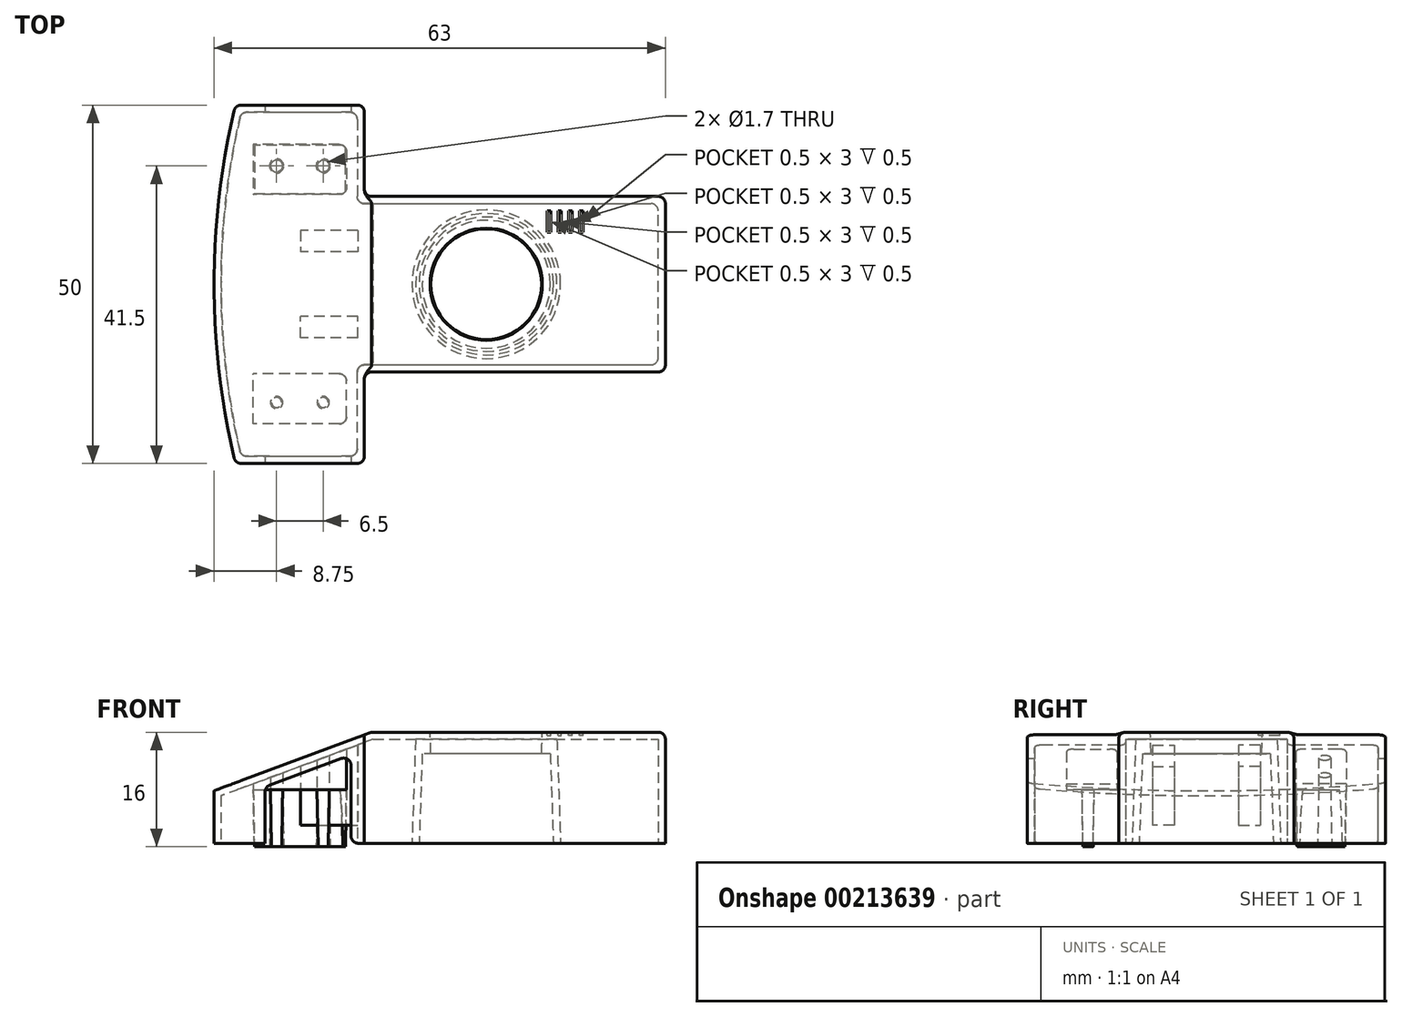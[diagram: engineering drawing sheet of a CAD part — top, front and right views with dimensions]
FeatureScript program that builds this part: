
annotation { "Feature Type Name" : "Feature", "Feature Type Description" : "" }
export const myFeature = defineFeature(function(context is Context, id is Id, definition is map)
    precondition{}
    {
        {
            var Q0;
            Q0=qCreatedBy(makeId("Top.planeOp"),FACE);
            var sketch = newSketch(context, id + "F0", { "sketchPlane" : qUnion([Q0])});
            skCircle(sketch, "E0", {"center": v(-4, 0) * mm, "radius": 9.37 * mm});
            skLineSegment(sketch, "E1.bottom", {"start": v(-21, -12.25) * mm, "end": v(21, -12.25) * mm});
            skLineSegment(sketch, "E1.top", {"start": v(-21, 12.25) * mm, "end": v(21, 12.25) * mm});
            skLineSegment(sketch, "E1.right", {"start": v(21, -12.25) * mm, "end": v(21, 12.25) * mm});
            skLineSegment(sketch, "E2.bottom", {"start": v(-21, -25) * mm, "end": v(-39, -25) * mm});
            skLineSegment(sketch, "E2.top", {"start": v(-21, 25) * mm, "end": v(-39, 25) * mm});
            skLineSegment(sketch, "E2.left", {"start": v(-21, -25) * mm, "end": v(-21, -12.25) * mm});
            skLineSegment(sketch, "E2.right", {"start": v(-39, -25) * mm, "end": v(-39, 25) * mm});
            skPoint(sketch, "E2.middle", {"position": v(-30, 0) * mm});
            skLineSegment(sketch, "E3.trimOffspring", {"start": v(-21, 12.25) * mm, "end": v(-21, 25) * mm});
            skLineSegment(sketch, "E4", {"start": v(-20, 12.25) * mm, "end": v(-20, -12.25) * mm});
            skPoint(sketch, "E5", {"position": v(-42, 0) * mm});
            skPoint(sketch, "E5.positionSnap0", {"position": v(-39, 0) * mm});
            skArc(sketch, "E6", {"start": v(-39, 25) * mm, "mid": v(-42, 0) * mm, "end": v(-39, -25) * mm});
            skSolve(sketch);
        }
        {
            var Q0;
            Q0=qSketchRegion(id+"F0",true);
            var Q1;
            Q1=makeQuery(id+"F0.imprint","IMPRINT",FACE,{"disambiguationData":[TD([[makeQuery(id+"F0.imprint","IMPRINT",EDGE,{"derivedFrom":sQuery(id+"F0.wireOp",EDGE,"E0")}),1.0]])]});
            extrude(context, id + "F1", {"entities" : qUnion([Q0, Q1]), "depth" : 15.5 * mm});
        }
        {
            var Q0;
            Q0=makeQuery(id+"F0.imprint","IMPRINT",FACE,{"disambiguationData":[TD([[makeQuery(id+"F0.imprint","IMPRINT",EDGE,{"derivedFrom":sQuery(id+"F0.wireOp",EDGE,"E0")}),1.0]])]});
            var Q1;
            Q1=makeQuery(id+"F1.opExtrude","CAP_FACE",FACE,{"disambiguationData":[OSD([sQuery(id+"F0.wireOp",EDGE,"E1.bottom"),sQuery(id+"F0.wireOp",EDGE,"E1.top"),sQuery(id+"F0.wireOp",EDGE,"E1.right"),sQuery(id+"F0.wireOp",EDGE,"E2.bottom"),sQuery(id+"F0.wireOp",EDGE,"E2.top"),sQuery(id+"F0.wireOp",EDGE,"E2.left"),sQuery(id+"F0.wireOp",EDGE,"E3.trimOffspring"),sQuery(id+"F0.wireOp",EDGE,"E6")])],"isStart":false});
            extrude(context, id + "F2", {"entities" : qUnion([Q0]), "operationType" : NewBodyOperationType.REMOVE, "endBound" : BoundingType.UP_TO_SURFACE, "endBoundEntityFace" : qUnion([Q1]), "depth" : 25 * mm, "hasDraft" : true, "draftAngle" : 2 * degree, "draftPullDirection" : true});
        }
        {
            var Q0;
            Q0=qCreatedBy(makeId("Front.planeOp"),FACE);
            var Q1;
            Q1=makeQuery(id+"F1.opExtrude","CAP_EDGE",EDGE,{"disambiguationData":[OSD([sQuery(id+"F0.wireOp",EDGE,"E2.bottom")])],"isStart":true});
            cPlane(context, id + "F3", {"entities" : qUnion([Q0, Q1]), "cplaneType" : CPlaneType.LINE_ANGLE, "offset" : 25 * mm, "angle" : 0 * degree, "width" : 150 * mm, "height" : 150 * mm});
        }
        {
            var Q0;
            Q0=qCreatedBy(id+"F3.planeOp",FACE);
            var sketch = newSketch(context, id + "F4", { "sketchPlane" : qUnion([Q0])});
            skLineSegment(sketch, "E7", {"start": v(20, 15.5) * mm, "end": v(42, 15.5) * mm});
            skLineSegment(sketch, "E8", {"start": v(42, 15.5) * mm, "end": v(42, 7.32) * mm});
            skLineSegment(sketch, "E9", {"start": v(42, 7.32) * mm, "end": v(20, 15.5) * mm});
            skLineSegment(sketch, "E10", {"start": v(42, 0) * mm, "end": v(41.46, 15.5) * mm, "construction": true});
            skLineSegment(sketch, "E11", {"start": v(42, 0) * mm, "end": v(42, 27.73) * mm, "construction": true});
            skSolve(sketch);
        }
        {
            var Q0;
            Q0=qSketchRegion(id+"F4",true);
            extrude(context, id + "F5", {"entities" : qUnion([Q0]), "operationType" : NewBodyOperationType.REMOVE, "endBound" : BoundingType.THROUGH_ALL, "depth" : 25 * mm});
        }
        {
            var Q0;
            Q0=makeQuery(id+"F1.opExtrude","CAP_FACE",FACE,{"disambiguationData":[OSD([sQuery(id+"F0.wireOp",EDGE,"E1.bottom"),sQuery(id+"F0.wireOp",EDGE,"E1.top"),sQuery(id+"F0.wireOp",EDGE,"E1.right"),sQuery(id+"F0.wireOp",EDGE,"E2.bottom"),sQuery(id+"F0.wireOp",EDGE,"E2.top"),sQuery(id+"F0.wireOp",EDGE,"E2.left"),sQuery(id+"F0.wireOp",EDGE,"E3.trimOffspring"),sQuery(id+"F0.wireOp",EDGE,"E6")])],"isStart":true});
            shell(context, id + "F6", {"entities" : qUnion([Q0]), "thickness" : 1 * mm});
        }
        {
            var Q0;
            Q0=makeQuery(id+"F1.opExtrude","SWEPT_FACE",FACE,{"disambiguationData":[OSD([sQuery(id+"F0.wireOp",EDGE,"E2.bottom")])]});
            var sketch = newSketch(context, id + "F7", { "sketchPlane" : qUnion([Q0])});
            skLineSegment(sketch, "E12", {"start": v(-20, 15.5) * mm, "end": v(-39, 8.43) * mm});
            skLineSegment(sketch, "E13", {"start": v(-39, 8.43) * mm, "end": v(-39, 15.5) * mm});
            skLineSegment(sketch, "E14", {"start": v(-39, 15.5) * mm, "end": v(-20, 15.5) * mm});
            skLineSegment(sketch, "E15", {"start": v(-34.87, 0) * mm, "end": v(-34.87, 7.86) * mm});
            skLineSegment(sketch, "E16", {"start": v(-34.87, 7.86) * mm, "end": v(-22.87, 12.32) * mm});
            skLineSegment(sketch, "E17", {"start": v(-22.87, 0) * mm, "end": v(-34.87, 0) * mm});
            skLineSegment(sketch, "E18", {"start": v(-22.87, 12.32) * mm, "end": v(-22.87, 0) * mm});
            skSolve(sketch);
        }
        {
            var Q0;
            Q0=makeQuery(id+"F7.imprint","IMPRINT",FACE,{"disambiguationData":[TD([[makeQuery(id+"F7.imprint","IMPRINT",EDGE,{"derivedFrom":sQuery(id+"F7.wireOp",EDGE,"E15")}),-1.0]])]});
            extrude(context, id + "F8", {"entities" : qUnion([Q0]), "operationType" : NewBodyOperationType.REMOVE, "endBound" : BoundingType.THROUGH_ALL, "oppositeDirection" : true, "depth" : 25 * mm});
        }
        {
            var Q0;
            Q0=makeQuery(id+"F1.opExtrude","CAP_FACE",FACE,{"disambiguationData":[OSD([sQuery(id+"F0.wireOp",EDGE,"E0"),sQuery(id+"F0.wireOp",EDGE,"E1.bottom"),sQuery(id+"F0.wireOp",EDGE,"E1.top"),sQuery(id+"F0.wireOp",EDGE,"E1.right"),sQuery(id+"F0.wireOp",EDGE,"E2.bottom"),sQuery(id+"F0.wireOp",EDGE,"E2.top"),sQuery(id+"F0.wireOp",EDGE,"E2.left"),sQuery(id+"F0.wireOp",EDGE,"E2.right"),sQuery(id+"F0.wireOp",EDGE,"E3.trimOffspring")])],"isStart":false});
            cPlane(context, id + "F9", {"entities" : qUnion([Q0]), "cplaneType" : CPlaneType.OFFSET, "offset" : 8 * mm, "oppositeDirection" : true, "width" : 150 * mm, "height" : 150 * mm});
        }
        {
            var Q0;
            Q0=qCreatedBy(id+"F9.planeOp",FACE);
            var sketch = newSketch(context, id + "F10", { "sketchPlane" : qUnion([Q0])});
            skLineSegment(sketch, "E19", {"start": v(0, 0) * mm, "end": v(-63, 0) * mm, "construction": true});
            skLineSegment(sketch, "E20.bottom", {"start": v(-36.5, -12.5) * mm, "end": v(-23.5, -12.5) * mm});
            skLineSegment(sketch, "E20.top", {"start": v(-36.5, -19.5) * mm, "end": v(-23.5, -19.5) * mm});
            skLineSegment(sketch, "E20.left", {"start": v(-36.5, -12.5) * mm, "end": v(-36.5, -19.5) * mm});
            skLineSegment(sketch, "E20.right", {"start": v(-23.5, -12.5) * mm, "end": v(-23.5, -19.5) * mm});
            skPoint(sketch, "E20.middle", {"position": v(-30, -16) * mm});
            skPoint(sketch, "E21", {"position": v(-33.25, -16.5) * mm});
            skPoint(sketch, "E22", {"position": v(-26.75, -16.5) * mm});
            skCircle(sketch, "E23", {"center": v(-33.25, -16.5) * mm, "radius": 0.85 * mm});
            skCircle(sketch, "E24", {"center": v(-26.75, -16.5) * mm, "radius": 0.85 * mm});
            skLineSegment(sketch, "E25.MirrorCS", {"start": v(-36.5, 12.5) * mm, "end": v(-23.5, 12.5) * mm});
            skLineSegment(sketch, "E26.MirrorCS", {"start": v(-36.5, 12.5) * mm, "end": v(-36.5, 19.5) * mm});
            skLineSegment(sketch, "E27.MirrorCS", {"start": v(-36.5, 19.5) * mm, "end": v(-23.5, 19.5) * mm});
            skLineSegment(sketch, "E28.MirrorCS", {"start": v(-23.5, 12.5) * mm, "end": v(-23.5, 19.5) * mm});
            skCircle(sketch, "E29.MirrorC", {"center": v(-26.75, 16.5) * mm, "radius": 0.85 * mm});
            skCircle(sketch, "E30.MirrorC", {"center": v(-33.25, 16.5) * mm, "radius": 0.85 * mm});
            skSolve(sketch);
        }
        {
            var Q0;
            Q0=makeQuery(id+"F10.imprint","IMPRINT",FACE,{"disambiguationData":[TD([[makeQuery(id+"F10.imprint","IMPRINT",EDGE,{"derivedFrom":sQuery(id+"F10.wireOp",EDGE,"E20.bottom")}),-1.0]])]});
            var Q1;
            Q1=makeQuery(id+"F10.imprint","IMPRINT",FACE,{"disambiguationData":[TD([[makeQuery(id+"F10.imprint","IMPRINT",EDGE,{"derivedFrom":sQuery(id+"F10.wireOp",EDGE,"E23")}),1.0]])]});
            var Q2;
            Q2=makeQuery(id+"F10.imprint","IMPRINT",FACE,{"disambiguationData":[TD([[makeQuery(id+"F10.imprint","IMPRINT",EDGE,{"derivedFrom":sQuery(id+"F10.wireOp",EDGE,"E24")}),1.0]])]});
            var Q3;
            Q3=makeQuery(id+"F10.imprint","IMPRINT",FACE,{"disambiguationData":[TD([[makeQuery(id+"F10.imprint","IMPRINT",EDGE,{"derivedFrom":sQuery(id+"F10.wireOp",EDGE,"E25.MirrorCS")}),1.0]])]});
            var Q4;
            Q4=makeQuery(id+"F10.imprint","IMPRINT",FACE,{"disambiguationData":[TD([[makeQuery(id+"F10.imprint","IMPRINT",EDGE,{"derivedFrom":sQuery(id+"F10.wireOp",EDGE,"E30.MirrorC")}),-1.0]])]});
            var Q5;
            Q5=makeQuery(id+"F10.imprint","IMPRINT",FACE,{"disambiguationData":[TD([[makeQuery(id+"F10.imprint","IMPRINT",EDGE,{"derivedFrom":sQuery(id+"F10.wireOp",EDGE,"E29.MirrorC")}),-1.0]])]});
            var Q6;
            Q6=makeQuery(id+"F6.opShell","OFFSET_FACE",FACE,{"disambiguationData":[OSD([sQuery(id+"F4.wireOp",EDGE,"E9")])]});
            extrude(context, id + "F11", {"entities" : qUnion([Q0, Q1, Q2, Q3, Q4, Q5]), "operationType" : NewBodyOperationType.ADD, "endBound" : BoundingType.UP_TO_SURFACE, "endBoundEntityFace" : qUnion([Q6]), "depth" : 25 * mm});
        }
        {
            var Q0;
            Q0=makeQuery(id+"F10.imprint","IMPRINT",FACE,{"disambiguationData":[TD([[makeQuery(id+"F10.imprint","IMPRINT",EDGE,{"derivedFrom":sQuery(id+"F10.wireOp",EDGE,"E23")}),1.0]])]});
            var Q1;
            Q1=makeQuery(id+"F10.imprint","IMPRINT",FACE,{"disambiguationData":[TD([[makeQuery(id+"F10.imprint","IMPRINT",EDGE,{"derivedFrom":sQuery(id+"F10.wireOp",EDGE,"E29.MirrorC")}),-1.0]])]});
            var Q2;
            Q2=makeQuery(id+"F10.imprint","IMPRINT",FACE,{"disambiguationData":[TD([[makeQuery(id+"F10.imprint","IMPRINT",EDGE,{"derivedFrom":sQuery(id+"F10.wireOp",EDGE,"E30.MirrorC")}),-1.0]])]});
            var Q3;
            Q3=makeQuery(id+"F10.imprint","IMPRINT",FACE,{"disambiguationData":[TD([[makeQuery(id+"F10.imprint","IMPRINT",EDGE,{"derivedFrom":sQuery(id+"F10.wireOp",EDGE,"E24")}),1.0]])]});
            extrude(context, id + "F12", {"entities" : qUnion([Q0, Q1, Q2, Q3]), "operationType" : NewBodyOperationType.ADD, "oppositeDirection" : true, "depth" : 8 * mm, "hasDraft" : true, "draftAngle" : 1 * degree, "draftPullDirection" : true});
        }
        {
            var Q0;
            Q0=makeQuery(id+"F1.opExtrude","CAP_EDGE",EDGE,{"disambiguationData":[OSD([sQuery(id+"F0.wireOp",EDGE,"E1.bottom")])],"isStart":false});
            var Q1;
            Q1=makeQuery(id+"F1.opExtrude","CAP_EDGE",EDGE,{"disambiguationData":[OSD([sQuery(id+"F0.wireOp",EDGE,"E1.right")])],"isStart":false});
            var Q2;
            Q2=makeQuery(id+"F1.opExtrude","CAP_EDGE",EDGE,{"disambiguationData":[OSD([sQuery(id+"F0.wireOp",EDGE,"E1.top")])],"isStart":false});
            var Q3;
            Q3=makeQuery(id+"F1.opExtrude","SWEPT_EDGE",EDGE,{"disambiguationData":[OSD([sQuery(id+"F0.wireOp",EDGE,"E1.bottom"),sQuery(id+"F0.wireOp",EDGE,"E1.right")])]});
            var Q4;
            Q4=makeQuery(id+"F1.opExtrude","SWEPT_EDGE",EDGE,{"disambiguationData":[OSD([sQuery(id+"F0.wireOp",EDGE,"E1.top"),sQuery(id+"F0.wireOp",EDGE,"E1.right")])]});
            fillet(context, id + "F13", {"entities" : qUnion([Q0, Q1, Q2, Q3, Q4]), "radius" : 1 * mm, "tangentPropagation" : true, "allowEdgeOverflow" : false});
        }
        {
            var Q0;
            Q0=makeQuery(id+"F1.opExtrude","SWEPT_EDGE",EDGE,{"disambiguationData":[OSD([sQuery(id+"F0.wireOp",EDGE,"E2.bottom"),sQuery(id+"F0.wireOp",EDGE,"E2.left")])]});
            var Q1;
            Q1=makeQuery(id+"F5.boolean.opBoolean","INTERSECT",EDGE,{"derivedFrom":[makeQuery(id+"F1.opExtrude","SWEPT_FACE",FACE,{"disambiguationData":[OSD([sQuery(id+"F0.wireOp",EDGE,"E2.left")])]}),makeQuery(id+"F5.opExtrude","SWEPT_FACE",FACE,{"disambiguationData":[OSD([sQuery(id+"FjstzwEYRuGCUyq_1.wireOp",EDGE,"6156deb2-2619-4c56-9df6-34b3699534c4")])]})]});
            var Q2;
            Q2=makeQuery(id+"F5.boolean.opBoolean","COPY",EDGE,{"derivedFrom":makeQuery(id+"F5.opExtrude","CAP_EDGE",EDGE,{"disambiguationData":[OSD([sQuery(id+"FjstzwEYRuGCUyq_1.wireOp",EDGE,"6156deb2-2619-4c56-9df6-34b3699534c4")])],"isStart":true})});
            var Q3;
            Q3=makeQuery(id+"F1.opExtrude","SWEPT_EDGE",EDGE,{"disambiguationData":[OSD([sQuery(id+"F0.wireOp",EDGE,"E2.bottom"),sQuery(id+"F0.wireOp",EDGE,"E2.right"),sQuery(id+"F0.wireOp",EDGE,"E6")])]});
            var Q4;
            Q4=makeQuery(id+"F5.boolean.opBoolean","INTERSECT",EDGE,{"derivedFrom":[makeQuery(id+"F1.opExtrude","SWEPT_FACE",FACE,{"disambiguationData":[OSD([sQuery(id+"F0.wireOp",EDGE,"E6")])]}),makeQuery(id+"F5.opExtrude","SWEPT_FACE",FACE,{"disambiguationData":[OSD([sQuery(id+"FjstzwEYRuGCUyq_1.wireOp",EDGE,"6156deb2-2619-4c56-9df6-34b3699534c4")])]})]});
            var Q5;
            Q5=makeQuery(id+"F5.boolean.opBoolean","INTERSECT",EDGE,{"derivedFrom":[makeQuery(id+"F1.opExtrude","SWEPT_FACE",FACE,{"disambiguationData":[OSD([sQuery(id+"F0.wireOp",EDGE,"E2.top")])]}),makeQuery(id+"F5.opExtrude","SWEPT_FACE",FACE,{"disambiguationData":[OSD([sQuery(id+"FjstzwEYRuGCUyq_1.wireOp",EDGE,"6156deb2-2619-4c56-9df6-34b3699534c4")])]})]});
            var Q6;
            Q6=makeQuery(id+"F1.opExtrude","SWEPT_EDGE",EDGE,{"disambiguationData":[OSD([sQuery(id+"F0.wireOp",EDGE,"E2.top"),sQuery(id+"F0.wireOp",EDGE,"E2.right"),sQuery(id+"F0.wireOp",EDGE,"E6")])]});
            var Q7;
            Q7=makeQuery(id+"F1.opExtrude","SWEPT_EDGE",EDGE,{"disambiguationData":[OSD([sQuery(id+"F0.wireOp",EDGE,"E2.top"),sQuery(id+"F0.wireOp",EDGE,"E3.trimOffspring")])]});
            var Q8;
            Q8=makeQuery(id+"F5.boolean.opBoolean","INTERSECT",EDGE,{"derivedFrom":[makeQuery(id+"F1.opExtrude","SWEPT_FACE",FACE,{"disambiguationData":[OSD([sQuery(id+"F0.wireOp",EDGE,"E3.trimOffspring")])]}),makeQuery(id+"F5.opExtrude","SWEPT_FACE",FACE,{"disambiguationData":[OSD([sQuery(id+"FjstzwEYRuGCUyq_1.wireOp",EDGE,"6156deb2-2619-4c56-9df6-34b3699534c4")])]})]});
            fillet(context, id + "F14", {"entities" : qUnion([Q0, Q1, Q2, Q3, Q4, Q5, Q6, Q7, Q8]), "radius" : 1 * mm, "tangentPropagation" : true, "allowEdgeOverflow" : false});
        }
        {
            var Q0;
            Q0=makeQuery(id+"F1.opExtrude","SWEPT_EDGE",EDGE,{"disambiguationData":[OSD([sQuery(id+"F0.wireOp",EDGE,"E1.top"),sQuery(id+"F0.wireOp",EDGE,"E3.trimOffspring")])]});
            fillet(context, id + "F15", {"entities" : qUnion([Q0]), "radius" : 1 * mm, "tangentPropagation" : true, "allowEdgeOverflow" : false});
        }
        {
            var Q0;
            Q0=makeQuery(id+"F1.opExtrude","SWEPT_EDGE",EDGE,{"disambiguationData":[OSD([sQuery(id+"F0.wireOp",EDGE,"E1.bottom"),sQuery(id+"F0.wireOp",EDGE,"E2.left")])]});
            var Q1;
            {var subQ0=sQuery(id+"F0.wireOp",EDGE,"E2.bottom");var subQ1=sQuery(id+"F7.wireOp",EDGE,"E18");Q1=makeQuery(id+"F8.boolean.opBoolean","COPY",EDGE,{"disambiguationData":[TD([makeQuery(id+"F1.opExtrude","SWEPT_FACE",FACE,{"disambiguationData":[OSD([subQ0])]})])],"derivedFrom":makeQuery(id+"F8.opExtrude","SWEPT_EDGE",EDGE,{"disambiguationData":[OSD([subQ0,sQuery(id+"F7.wireOp",EDGE,"E17"),subQ1])]})});}
            var Q2;
            {var subQ0=sQuery(id+"F0.wireOp",EDGE,"E2.bottom");var subQ1=sQuery(id+"F7.wireOp",EDGE,"E15");Q2=makeQuery(id+"F8.boolean.opBoolean","COPY",EDGE,{"disambiguationData":[TD([makeQuery(id+"F1.opExtrude","SWEPT_FACE",FACE,{"disambiguationData":[OSD([subQ0])]})])],"derivedFrom":makeQuery(id+"F8.opExtrude","SWEPT_EDGE",EDGE,{"disambiguationData":[OSD([subQ0,subQ1,sQuery(id+"F7.wireOp",EDGE,"E17")])]})});}
            var Q3;
            {var subQ0=sQuery(id+"F0.wireOp",EDGE,"E2.top");var subQ1=sQuery(id+"F0.wireOp",EDGE,"E2.bottom");var subQ2=sQuery(id+"F7.wireOp",EDGE,"E15");Q3=makeQuery(id+"F8.boolean.opBoolean","COPY",EDGE,{"disambiguationData":[TD([makeQuery(id+"F1.opExtrude","SWEPT_FACE",FACE,{"disambiguationData":[OSD([subQ0])]})])],"derivedFrom":makeQuery(id+"F8.opExtrude","SWEPT_EDGE",EDGE,{"disambiguationData":[OSD([subQ1,subQ2,sQuery(id+"F7.wireOp",EDGE,"E17")])]})});}
            var Q4;
            {var subQ0=sQuery(id+"F0.wireOp",EDGE,"E2.top");var subQ1=sQuery(id+"F0.wireOp",EDGE,"E2.bottom");var subQ2=sQuery(id+"F7.wireOp",EDGE,"E18");Q4=makeQuery(id+"F8.boolean.opBoolean","COPY",EDGE,{"disambiguationData":[TD([makeQuery(id+"F1.opExtrude","SWEPT_FACE",FACE,{"disambiguationData":[OSD([subQ0])]})])],"derivedFrom":makeQuery(id+"F8.opExtrude","SWEPT_EDGE",EDGE,{"disambiguationData":[OSD([subQ1,sQuery(id+"F7.wireOp",EDGE,"E17"),subQ2])]})});}
            var Q5;
            {var subQ0=sQuery(id+"F0.wireOp",EDGE,"E2.top");var subQ1=sQuery(id+"F7.wireOp",EDGE,"E18");var subQ2=sQuery(id+"F7.wireOp",EDGE,"E16");Q5=makeQuery(id+"F8.boolean.opBoolean","COPY",EDGE,{"disambiguationData":[TD([makeQuery(id+"F1.opExtrude","SWEPT_FACE",FACE,{"disambiguationData":[OSD([subQ0])]})])],"derivedFrom":makeQuery(id+"F8.opExtrude","SWEPT_EDGE",EDGE,{"disambiguationData":[OSD([subQ2,subQ1])]})});}
            var Q6;
            {var subQ0=sQuery(id+"F0.wireOp",EDGE,"E2.top");var subQ1=sQuery(id+"F7.wireOp",EDGE,"E15");var subQ2=sQuery(id+"F7.wireOp",EDGE,"E16");Q6=makeQuery(id+"F8.boolean.opBoolean","COPY",EDGE,{"disambiguationData":[TD([makeQuery(id+"F1.opExtrude","SWEPT_FACE",FACE,{"disambiguationData":[OSD([subQ0])]})])],"derivedFrom":makeQuery(id+"F8.opExtrude","SWEPT_EDGE",EDGE,{"disambiguationData":[OSD([subQ1,subQ2])]})});}
            var Q7;
            {var subQ0=sQuery(id+"F0.wireOp",EDGE,"E2.bottom");var subQ1=sQuery(id+"F7.wireOp",EDGE,"E18");var subQ2=sQuery(id+"F7.wireOp",EDGE,"E16");Q7=makeQuery(id+"F8.boolean.opBoolean","COPY",EDGE,{"disambiguationData":[TD([makeQuery(id+"F1.opExtrude","SWEPT_FACE",FACE,{"disambiguationData":[OSD([subQ0])]})])],"derivedFrom":makeQuery(id+"F8.opExtrude","SWEPT_EDGE",EDGE,{"disambiguationData":[OSD([subQ2,subQ1])]})});}
            var Q8;
            {var subQ0=sQuery(id+"F0.wireOp",EDGE,"E2.bottom");var subQ1=sQuery(id+"F7.wireOp",EDGE,"E15");var subQ2=sQuery(id+"F7.wireOp",EDGE,"E16");Q8=makeQuery(id+"F8.boolean.opBoolean","COPY",EDGE,{"disambiguationData":[TD([makeQuery(id+"F1.opExtrude","SWEPT_FACE",FACE,{"disambiguationData":[OSD([subQ0])]})])],"derivedFrom":makeQuery(id+"F8.opExtrude","SWEPT_EDGE",EDGE,{"disambiguationData":[OSD([subQ1,subQ2])]})});}
            var Q9;
            Q9=makeQuery(id+"F6.opShell","OFFSET_EDGE",EDGE,{"disambiguationData":[OSD([sQuery(id+"F0.wireOp",EDGE,"E1.top"),sQuery(id+"F0.wireOp",EDGE,"E3.trimOffspring")])]});
            var Q10;
            Q10=makeQuery(id+"F6.opShell","OFFSET_EDGE",EDGE,{"disambiguationData":[OSD([sQuery(id+"F0.wireOp",EDGE,"E1.bottom"),sQuery(id+"F0.wireOp",EDGE,"E2.left")])]});
            fillet(context, id + "F16", {"entities" : qUnion([Q0, Q1, Q2, Q3, Q4, Q5, Q6, Q7, Q8, Q9, Q10]), "radius" : 1 * mm, "tangentPropagation" : true, "allowEdgeOverflow" : false});
        }
        {
            var Q0;
            Q0=makeQuery(id+"F6.opShell","OFFSET_EDGE",EDGE,{"disambiguationData":[OSD([sQuery(id+"F0.wireOp",EDGE,"E1.top"),sQuery(id+"F0.wireOp",EDGE,"E1.right")])]});
            var Q1;
            Q1=makeQuery(id+"F6.opShell","OFFSET_EDGE",EDGE,{"disambiguationData":[OSD([sQuery(id+"F0.wireOp",EDGE,"E1.bottom"),sQuery(id+"F0.wireOp",EDGE,"E1.right")])]});
            var Q2;
            {var subQ0=sQuery(id+"F0.wireOp",EDGE,"E0");Q2=makeQuery(id+"F6.opShell","OFFSET_EDGE",EDGE,{"disambiguationData":[OSD([subQ0]),TDD([makeQuery(id+"F1.opExtrude","CAP_EDGE",EDGE,{"disambiguationData":[OSD([subQ0])],"isStart":false})])]});}
            var Q3;
            Q3=makeQuery(id+"F6.opShell","OFFSET_EDGE",EDGE,{"disambiguationData":[OSD([sQuery(id+"F0.wireOp",EDGE,"E2.top"),sQuery(id+"F0.wireOp",EDGE,"E3.trimOffspring")])]});
            var Q4;
            Q4=makeQuery(id+"F6.opShell","OFFSET_EDGE",EDGE,{"disambiguationData":[OSD([sQuery(id+"F0.wireOp",EDGE,"E2.top"),sQuery(id+"F0.wireOp",EDGE,"E2.right"),sQuery(id+"F0.wireOp",EDGE,"E6")])]});
            var Q5;
            Q5=makeQuery(id+"F6.opShell","OFFSET_EDGE",EDGE,{"disambiguationData":[OSD([sQuery(id+"F0.wireOp",EDGE,"E2.bottom"),sQuery(id+"F0.wireOp",EDGE,"E2.left")])]});
            var Q6;
            Q6=makeQuery(id+"F6.opShell","OFFSET_EDGE",EDGE,{"disambiguationData":[OSD([sQuery(id+"F0.wireOp",EDGE,"E2.bottom"),sQuery(id+"F0.wireOp",EDGE,"E2.right"),sQuery(id+"F0.wireOp",EDGE,"E6")])]});
            var Q7;
            Q7=makeQuery(id+"F11.opExtrude","SWEPT_EDGE",EDGE,{"disambiguationData":[OSD([sQuery(id+"F10.wireOp",EDGE,"E20.bottom"),sQuery(id+"F10.wireOp",EDGE,"E20.right")])]});
            var Q8;
            Q8=makeQuery(id+"F11.opExtrude","SWEPT_EDGE",EDGE,{"disambiguationData":[OSD([sQuery(id+"F10.wireOp",EDGE,"E20.top"),sQuery(id+"F10.wireOp",EDGE,"E20.right")])]});
            var Q9;
            Q9=makeQuery(id+"F11.opExtrude","SWEPT_EDGE",EDGE,{"disambiguationData":[OSD([sQuery(id+"F10.wireOp",EDGE,"E27.MirrorCS"),sQuery(id+"F10.wireOp",EDGE,"E28.MirrorCS")])]});
            var Q10;
            Q10=makeQuery(id+"F11.opExtrude","SWEPT_EDGE",EDGE,{"disambiguationData":[OSD([sQuery(id+"F10.wireOp",EDGE,"E25.MirrorCS"),sQuery(id+"F10.wireOp",EDGE,"E28.MirrorCS")])]});
            fillet(context, id + "F17", {"entities" : qUnion([Q0, Q1, Q2, Q3, Q4, Q5, Q6, Q7, Q8, Q9, Q10]), "radius" : 1 * mm, "tangentPropagation" : true, "allowEdgeOverflow" : false});
        }
        {
            var Q0;
            Q0=qCreatedBy(id+"F9.planeOp",FACE);
            var sketch = newSketch(context, id + "F18", { "sketchPlane" : qUnion([Q0])});
            skPoint(sketch, "E31", {"position": v(-29.94, -4.5) * mm});
            skLineSegment(sketch, "E32.bottom", {"start": v(-29.94, -4.5) * mm, "end": v(-21.94, -4.5) * mm});
            skLineSegment(sketch, "E32.top", {"start": v(-29.94, -7.5) * mm, "end": v(-21.94, -7.5) * mm});
            skLineSegment(sketch, "E32.left", {"start": v(-29.94, -4.5) * mm, "end": v(-29.94, -7.5) * mm});
            skLineSegment(sketch, "E32.right", {"start": v(-21.94, -4.5) * mm, "end": v(-21.94, -7.5) * mm});
            skLineSegment(sketch, "E33", {"start": v(0, 0) * mm, "end": v(-48.4, 0) * mm, "construction": true});
            skLineSegment(sketch, "E34.MirrorCS", {"start": v(-29.94, 4.5) * mm, "end": v(-21.94, 4.5) * mm});
            skLineSegment(sketch, "E35.MirrorCS", {"start": v(-21.94, 4.5) * mm, "end": v(-21.94, 7.5) * mm});
            skLineSegment(sketch, "E36.MirrorCS", {"start": v(-29.94, 7.5) * mm, "end": v(-21.94, 7.5) * mm});
            skLineSegment(sketch, "E37.MirrorCS", {"start": v(-29.94, 4.5) * mm, "end": v(-29.94, 7.5) * mm});
            skSolve(sketch);
        }
        {
            var Q0;
            Q0=qSketchRegion(id+"F18",true);
            var Q1;
            Q1=makeQuery(id+"F6.opShell","OFFSET_FACE",FACE,{"disambiguationData":[OSD([sQuery(id+"F4.wireOp",EDGE,"E9")])]});
            extrude(context, id + "F19", {"entities" : qUnion([Q0]), "operationType" : NewBodyOperationType.ADD, "endBound" : BoundingType.UP_TO_SURFACE, "endBoundEntityFace" : qUnion([Q1]), "depth" : 25 * mm, "hasSecondDirection" : true, "secondDirectionOppositeDirection" : true, "secondDirectionDepth" : 5 * mm});
        }
        {
            var Q0;
            Q0=makeQuery(id+"F1.opExtrude","CAP_FACE",FACE,{"disambiguationData":[OSD([sQuery(id+"F0.wireOp",EDGE,"E1.bottom"),sQuery(id+"F0.wireOp",EDGE,"E1.top"),sQuery(id+"F0.wireOp",EDGE,"E1.right"),sQuery(id+"F0.wireOp",EDGE,"E2.bottom"),sQuery(id+"F0.wireOp",EDGE,"E2.top"),sQuery(id+"F0.wireOp",EDGE,"E2.left"),sQuery(id+"F0.wireOp",EDGE,"E3.trimOffspring"),sQuery(id+"F0.wireOp",EDGE,"E6")])],"isStart":false});
            var sketch = newSketch(context, id + "F20", { "sketchPlane" : qUnion([Q0])});
            skCircle(sketch, "E38", {"center": v(-4, 0) * mm, "radius": 8.83 * mm});
            skCircle(sketch, "E39.0", {"center": v(-4, 0) * mm, "radius": 7.83 * mm});
            skSolve(sketch);
        }
        {
            var Q0;
            Q0=qSketchRegion(id+"F20",true);
            extrude(context, id + "F21", {"entities" : qUnion([Q0]), "operationType" : NewBodyOperationType.ADD, "oppositeDirection" : true, "depth" : 3 * mm, "hasDraft" : true, "draftAngle" : 2 * degree});
        }
        {
            var Q0;
            Q0=makeQuery(id+"F21.boolean.opBoolean","MERGE",FACE,{"derivedFrom":[makeQuery(id+"F1.opExtrude","CAP_FACE",FACE,{"disambiguationData":[OSD([sQuery(id+"F0.wireOp",EDGE,"E1.bottom"),sQuery(id+"F0.wireOp",EDGE,"E1.top"),sQuery(id+"F0.wireOp",EDGE,"E1.right"),sQuery(id+"F0.wireOp",EDGE,"E2.bottom"),sQuery(id+"F0.wireOp",EDGE,"E2.top"),sQuery(id+"F0.wireOp",EDGE,"E2.left"),sQuery(id+"F0.wireOp",EDGE,"E3.trimOffspring"),sQuery(id+"F0.wireOp",EDGE,"E6")])],"isStart":false}),makeQuery(id+"F21.opExtrude","CAP_FACE",FACE,{"disambiguationData":[OSD([sQuery(id+"F20.wireOp",EDGE,"E38"),sQuery(id+"F20.wireOp",EDGE,"E39.0")])],"isStart":true})]});
            var sketch = newSketch(context, id + "F22", { "sketchPlane" : qUnion([Q0])});
            skLineSegment(sketch, "E40.bottom", {"start": v(4.5, 10.25) * mm, "end": v(5, 10.25) * mm});
            skLineSegment(sketch, "E40.top", {"start": v(4.5, 7.25) * mm, "end": v(5, 7.25) * mm});
            skLineSegment(sketch, "E40.left", {"start": v(4.5, 10.25) * mm, "end": v(4.5, 7.25) * mm});
            skLineSegment(sketch, "E40.right", {"start": v(5, 10.25) * mm, "end": v(5, 7.25) * mm});
            skLineSegment(sketch, "E41.bottom", {"start": v(6, 10.25) * mm, "end": v(6.5, 10.25) * mm});
            skLineSegment(sketch, "E41.top", {"start": v(6, 7.25) * mm, "end": v(6.5, 7.25) * mm});
            skLineSegment(sketch, "E41.left", {"start": v(6, 10.25) * mm, "end": v(6, 7.25) * mm});
            skLineSegment(sketch, "E41.right", {"start": v(6.5, 10.25) * mm, "end": v(6.5, 7.25) * mm});
            skLineSegment(sketch, "E42", {"start": v(7, 10.25) * mm, "end": v(7, 7.32) * mm, "construction": true});
            skLineSegment(sketch, "E43.MirrorCS", {"start": v(7.5, 10.25) * mm, "end": v(7.5, 7.25) * mm});
            skLineSegment(sketch, "E44.MirrorCS", {"start": v(8, 10.25) * mm, "end": v(7.5, 10.25) * mm});
            skLineSegment(sketch, "E45.MirrorCS", {"start": v(8, 7.25) * mm, "end": v(7.5, 7.25) * mm});
            skLineSegment(sketch, "E46.MirrorCS", {"start": v(8, 10.25) * mm, "end": v(8, 7.25) * mm});
            skLineSegment(sketch, "E47.MirrorCS", {"start": v(9, 10.25) * mm, "end": v(9, 7.25) * mm});
            skLineSegment(sketch, "E48.MirrorCS", {"start": v(9.5, 7.25) * mm, "end": v(9, 7.25) * mm});
            skLineSegment(sketch, "E49.MirrorCS", {"start": v(9.5, 10.25) * mm, "end": v(9, 10.25) * mm});
            skLineSegment(sketch, "E50.MirrorCS", {"start": v(9.5, 10.25) * mm, "end": v(9.5, 7.25) * mm});
            skSolve(sketch);
        }
        {
            var Q0;
            Q0=qSketchRegion(id+"F22",true);
            extrude(context, id + "F23", {"entities" : qUnion([Q0]), "operationType" : NewBodyOperationType.REMOVE, "oppositeDirection" : true, "depth" : 0.5 * mm});
        }
    });
